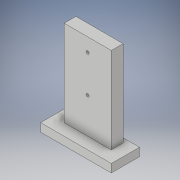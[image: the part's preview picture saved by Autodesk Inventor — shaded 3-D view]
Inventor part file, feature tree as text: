
AUTODESK INVENTOR PART (.ipt)
format: ipt  version: 2017 (Build 210142000, 142)  size: 129,536 bytes
history: native  units: in
note: dims shown in document units (in); Inventor stores cm internally (conversion verified against a paired STEP export)
features: extrude x3, sketch x3
ambient origin geometry x8: Origin, YZ Plane, XZ Plane, XY Plane, X Axis, Y Axis, Z Axis, Center Point
bodies: Solid1 (feature_tree)
feature tree (6):
  extrude  "Extrusion1"  Depth=1.575in
  extrude  "Extrusion3"  Depth=0.122in
  extrude  "Extrusion4"  Depth=0.193in
  sketch  "Sketch1"  dims[d0=1.575in d1=0.6in]
  sketch  "Sketch3"  dims[d2=2.4in d3=0.122in]
  sketch  "Sketch5"  dims[d4=0.122in d5=0.57in d6=1.0in d7=1.0in d8=4.0in d9=0.5in d10=0.5in d11=0.35in d12=0.5in d13=0.0in d16=0.5in d17=0.0in d18=0.193in d19=0.0in]
